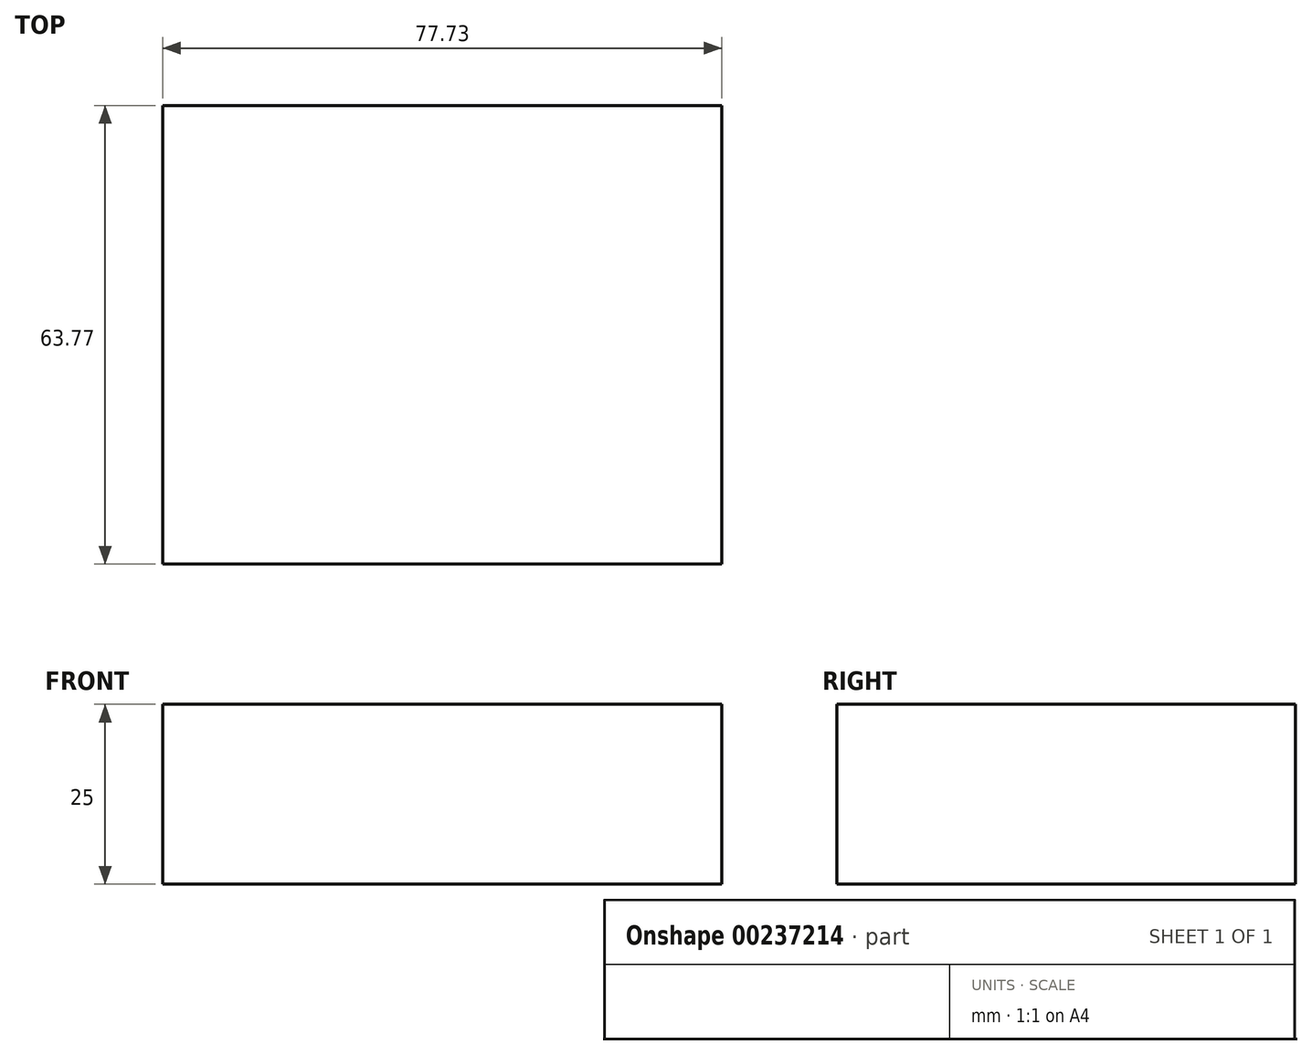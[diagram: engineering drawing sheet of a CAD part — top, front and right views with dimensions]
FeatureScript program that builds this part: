
annotation { "Feature Type Name" : "Feature", "Feature Type Description" : "" }
export const myFeature = defineFeature(function(context is Context, id is Id, definition is map)
    precondition{}
    {
        {
            var Q0;
            Q0=qCreatedBy(makeId("Top.planeOp"),FACE);
            var sketch = newSketch(context, id + "F0", { "sketchPlane" : qUnion([Q0])});
            skLineSegment(sketch, "E0.bottom", {"start": v(0, 0) * mm, "end": v(77.73, 0) * mm});
            skLineSegment(sketch, "E0.top", {"start": v(0, 63.77) * mm, "end": v(77.73, 63.77) * mm});
            skLineSegment(sketch, "E0.left", {"start": v(0, 0) * mm, "end": v(0, 63.77) * mm});
            skLineSegment(sketch, "E0.right", {"start": v(77.73, 0) * mm, "end": v(77.73, 63.77) * mm});
            skSolve(sketch);
        }
        {
            var Q0;
            Q0=makeQuery(id+"F0.imprint","IMPRINT",FACE,{"disambiguationData":[TD([[makeQuery(id+"F0.imprint","IMPRINT",EDGE,{"derivedFrom":sQuery(id+"F0.wireOp",EDGE,"E0.bottom")}),1.0]])]});
            extrude(context, id + "F1", {"entities" : qUnion([Q0]), "depth" : 25 * mm});
        }
    });
